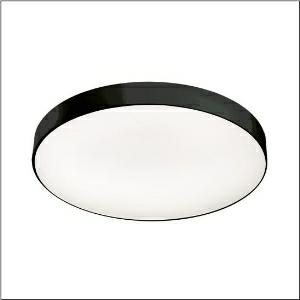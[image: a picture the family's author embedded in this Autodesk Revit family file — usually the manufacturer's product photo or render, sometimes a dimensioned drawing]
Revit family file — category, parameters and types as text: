
# Revit family: round_21_l_51mr38nd0421b
name_source: partatom
category: Lighting Fixtures
units: mm (PartAtom-declared; Revit-internal decimal feet)

## family parameters
Cut with Voids When Loaded = No
Host = Face
Light Source = No
Part Type = Normal
Room Calculation Point = No
Round Connector Dimension = Use Diameter
Shared = No

## types (1)
- Round 21 L (1 x LED, 12230 lm, 88.2 W, 4000K)
    Apparent Load = 88 VA
    CIE Flux Codes = 66 90 98 71 100
    Color Rendering = 80
    Color Temperature = 4000K
    Default Elevation = 1800 mm
    Description = Round 21 L, wall and ceiling luminaire, primary optical cover: micro prismatic cover, of PMMA, transparent, CAT 2 (L<= 3000cd/m²), light emission: direct/indirect distribution, primary light characteristic: symmetric, installation type: suspended mounting, surface-mounted, LED, rated luminous flux: 12.230lm, luminous efficacy: 139lm/W, light colour: 840, colour temperature: 4000K, control gear: DALI 2, with terminal, 5-pole, mains connection: 230V, AC, 50/60Hz, rated input power: 88W, housing, of aluminium, coated, black, diameter: 850mm, height: 62mm, protection rating (complete): IP40, insulation class (complete): insulation class I (protective earthing), certification: CE, impact resistance: IK04, permissible operating ambient temperature: -10..+35°C, packaging unit: 1 piece
    Height = 87 mm
    Lamp = 1 x LED
    Lamp Light Flux = 12230 lm
    Lamp Power = 88.2 W
    Lamp count = 1
    Length = 850 mm
    Luminous efficacy = 139 lm/W
    Manufacturer = Siteco
    ModVariant = No
    Model = 51MR38ND0421B
    Mounting Place = Ceiling
    Mounting Type = Surface mounted
    Number of Poles = 1
    OnlyDefault = Yes
    Power Factor = 1
    Product Name = Round 21 L
    Product group = wall and ceiling luminaire | ceiling mounted
    ProductGroupID = 305
    Protection Class = Protection class I
    Protection Degree = IP 40
    RLX_Detail_Level = 1
    RLX_Emergency_Light_Flux = 0 lm
    RLX_Emergency_Type = 0
    RLX_Emergency_Type_DB = No
    RlxData = <blob elided: 28757 chars, md5=d89de25d>
    Socket = socket
    Standby Power = 0 W
    System Light Flux = 12230 lm
    System Power = 88 W
    Type Comments = Product without accessories
    Type Image = l_1258326.jpg
    URL = http://relux.com
    VarID = ---
    Voltage = 0 V
    Weight = 0.00 kg
    Width = 0 mm  [stored 0 ft]

note: [stored X ft] marks values corroborated as IEEE doubles in the binary element streams (Revit-internal decimal feet)

## geometry (parser evidence)
native form markers: Blend x4, Sweep x12
no freeform markers — native parametric forms only
